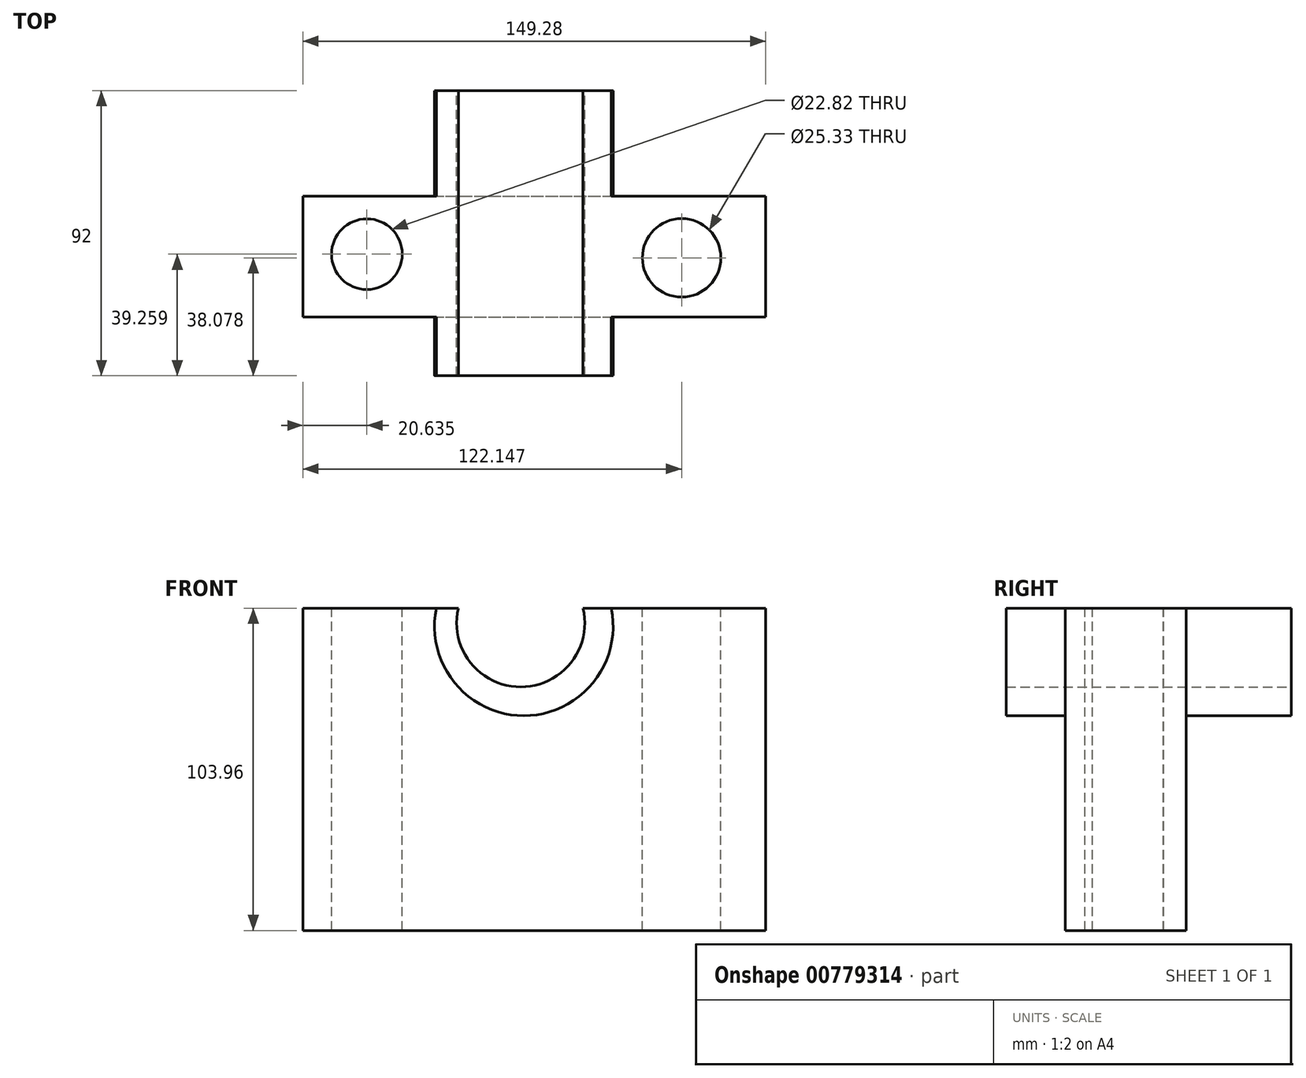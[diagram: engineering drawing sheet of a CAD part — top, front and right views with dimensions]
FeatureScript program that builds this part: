
annotation { "Feature Type Name" : "Feature", "Feature Type Description" : "" }
export const myFeature = defineFeature(function(context is Context, id is Id, definition is map)
    precondition{}
    {
        {
            var Q0;
            Q0=qCreatedBy(makeId("Front.planeOp"),FACE);
            var sketch = newSketch(context, id + "F0", { "sketchPlane" : qUnion([Q0])});
            skLineSegment(sketch, "E0.bottom", {"start": v(-74.64, 55.1) * mm, "end": v(-24.5, 55.1) * mm});
            skLineSegment(sketch, "E0.top", {"start": v(-74.64, -48.86) * mm, "end": v(74.64, -48.86) * mm});
            skLineSegment(sketch, "E0.left", {"start": v(-74.64, 55.1) * mm, "end": v(-74.64, -48.86) * mm});
            skLineSegment(sketch, "E0.right", {"start": v(74.64, 55.1) * mm, "end": v(74.64, -48.86) * mm});
            skArc(sketch, "E1", {"start": v(-31.58, 55.1) * mm, "mid": v(-3.4, 20.43) * mm, "end": v(24.79, 55.1) * mm});
            skArc(sketch, "E2", {"start": v(-24.5, 55.1) * mm, "mid": v(-4.4, 29.72) * mm, "end": v(15.72, 55.1) * mm});
            skLineSegment(sketch, "E3.trimOffspring", {"start": v(15.72, 55.1) * mm, "end": v(74.64, 55.1) * mm});
            skSolve(sketch);
        }
        {
            var Q0;
            {var subQ2=sQuery(id+"F0.wireOp",EDGE,"E1");Q0=makeQuery(id+"F0.imprint","IMPRINT",FACE,{"disambiguationData":[TD([[makeQuery(id+"F0.imprint","IMPRINT",EDGE,{"derivedFrom":subQ2}),1.0]])]});}
            extrude(context, id + "F1", {"entities" : qUnion([Q0]), "depth" : 19 * mm, "offsetDistance" : 25 * mm});
        }
        {
            var Q0;
            Q0=makeQuery(id+"F1.opExtrude","CAP_FACE",FACE,{"disambiguationData":[OSD([sQuery(id+"F0.wireOp",EDGE,"E0.bottom"),sQuery(id+"F0.wireOp",EDGE,"E1"),sQuery(id+"F0.wireOp",EDGE,"E2"),sQuery(id+"F0.wireOp",EDGE,"E3.trimOffspring")])],"isStart":false});
            extrude(context, id + "F2", {"entities" : qUnion([Q0]), "operationType" : NewBodyOperationType.ADD, "oppositeDirection" : true, "depth" : 92 * mm, "offsetDistance" : 25 * mm});
        }
        {
            var Q0;
            Q0=makeQuery(id+"F0.imprint","IMPRINT",FACE,{"disambiguationData":[TD([[makeQuery(id+"F0.imprint","IMPRINT",EDGE,{"derivedFrom":sQuery(id+"F0.wireOp",EDGE,"E0.top")}),1.0]])]});
            extrude(context, id + "F3", {"entities" : qUnion([Q0]), "operationType" : NewBodyOperationType.ADD, "oppositeDirection" : true, "depth" : 39 * mm, "offsetDistance" : 25 * mm});
        }
        {
            var Q0;
            {var subQ0=sQuery(id+"F0.wireOp",EDGE,"E0.bottom");Q0=makeQuery(id+"F3.boolean.opBoolean","MERGE",FACE,{"derivedFrom":[makeQuery(id+"F2.boolean.opBoolean","MERGE",FACE,{"derivedFrom":[makeQuery(id+"F1.opExtrude","SWEPT_FACE",FACE,{"disambiguationData":[OSD([subQ0])]}),makeQuery(id+"F2.opExtrude","SWEPT_FACE",FACE,{"disambiguationData":[OSD([subQ0])]})]}),makeQuery(id+"F3.opExtrude","SWEPT_FACE",FACE,{"disambiguationData":[OSD([subQ0])]})]});}
            var sketch = newSketch(context, id + "F4", { "sketchPlane" : qUnion([Q0])});
            skCircle(sketch, "E4", {"center": v(-54, 20.26) * mm, "radius": 11.4 * mm});
            skSolve(sketch);
        }
        {
            var Q0;
            {var subQ0=sQuery(id+"F0.wireOp",EDGE,"E3.trimOffspring");Q0=makeQuery(id+"F3.boolean.opBoolean","MERGE",FACE,{"derivedFrom":[makeQuery(id+"F2.boolean.opBoolean","MERGE",FACE,{"derivedFrom":[makeQuery(id+"F1.opExtrude","SWEPT_FACE",FACE,{"disambiguationData":[OSD([subQ0])]}),makeQuery(id+"F2.opExtrude","SWEPT_FACE",FACE,{"disambiguationData":[OSD([subQ0])]})]}),makeQuery(id+"F3.opExtrude","SWEPT_FACE",FACE,{"disambiguationData":[OSD([subQ0])]})]});}
            var sketch = newSketch(context, id + "F5", { "sketchPlane" : qUnion([Q0])});
            skCircle(sketch, "E5", {"center": v(47.5, 19.08) * mm, "radius": 12.66 * mm});
            skSolve(sketch);
        }
        {
            var Q0;
            Q0=makeQuery(id+"F4.imprint","IMPRINT",FACE,{"disambiguationData":[TD([[makeQuery(id+"F4.imprint","IMPRINT",EDGE,{"derivedFrom":sQuery(id+"F4.wireOp",EDGE,"E4")}),1.0]])]});
            extrude(context, id + "F6", {"entities" : qUnion([Q0]), "operationType" : NewBodyOperationType.REMOVE, "endBound" : BoundingType.THROUGH_ALL, "oppositeDirection" : true, "depth" : 25 * mm, "offsetDistance" : 25 * mm});
        }
        {
            var Q0;
            Q0=makeQuery(id+"F5.imprint","IMPRINT",FACE,{"disambiguationData":[TD([[makeQuery(id+"F5.imprint","IMPRINT",EDGE,{"derivedFrom":sQuery(id+"F5.wireOp",EDGE,"E5")}),1.0]])]});
            extrude(context, id + "F7", {"entities" : qUnion([Q0]), "operationType" : NewBodyOperationType.REMOVE, "endBound" : BoundingType.THROUGH_ALL, "oppositeDirection" : true, "depth" : 25 * mm, "offsetDistance" : 25 * mm});
        }
    });
